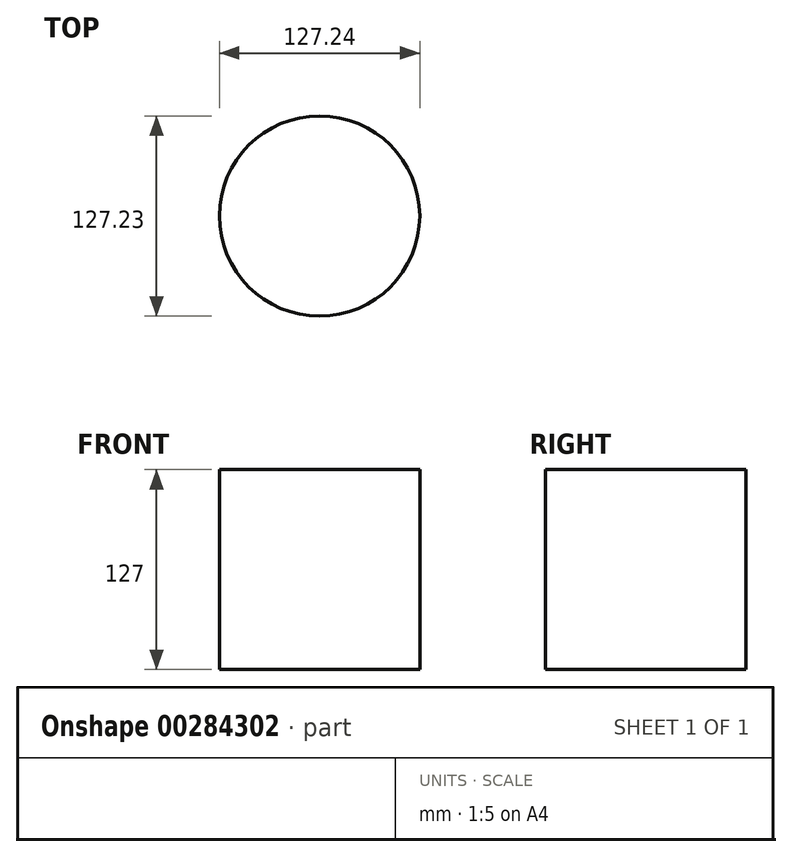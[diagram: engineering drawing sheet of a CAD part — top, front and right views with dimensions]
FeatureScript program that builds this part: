
annotation { "Feature Type Name" : "Feature", "Feature Type Description" : "" }
export const myFeature = defineFeature(function(context is Context, id is Id, definition is map)
    precondition{}
    {
        {
            var Q0;
            Q0=qCreatedBy(makeId("Top.planeOp"),FACE);
            var sketch = newSketch(context, id + "F0", { "sketchPlane" : qUnion([Q0])});
            skPoint(sketch, "E0.middle", {"position": v(0, 1.66) * mm});
            skCircle(sketch, "E1", {"center": v(0, 1.66) * mm, "radius": 63.62 * mm});
            skSolve(sketch);
        }
        {
            var Q0;
            Q0=makeQuery(id+"F0.imprint","IMPRINT",FACE,{"disambiguationData":[TD([[makeQuery(id+"F0.imprint","IMPRINT",EDGE,{"derivedFrom":sQuery(id+"F0.wireOp",EDGE,"E0.bottom")}),1.0]])]});
            var Q1;
            Q1=makeQuery(id+"F0.imprint","IMPRINT",FACE,{"disambiguationData":[TD([[makeQuery(id+"F0.imprint","IMPRINT",EDGE,{"derivedFrom":sQuery(id+"F0.wireOp",EDGE,"E1")}),1.0]])]});
            extrude(context, id + "F1", {"entities" : qUnion([Q0, Q1]), "oppositeDirection" : true, "depth" : 127 * mm});
        }
    });
